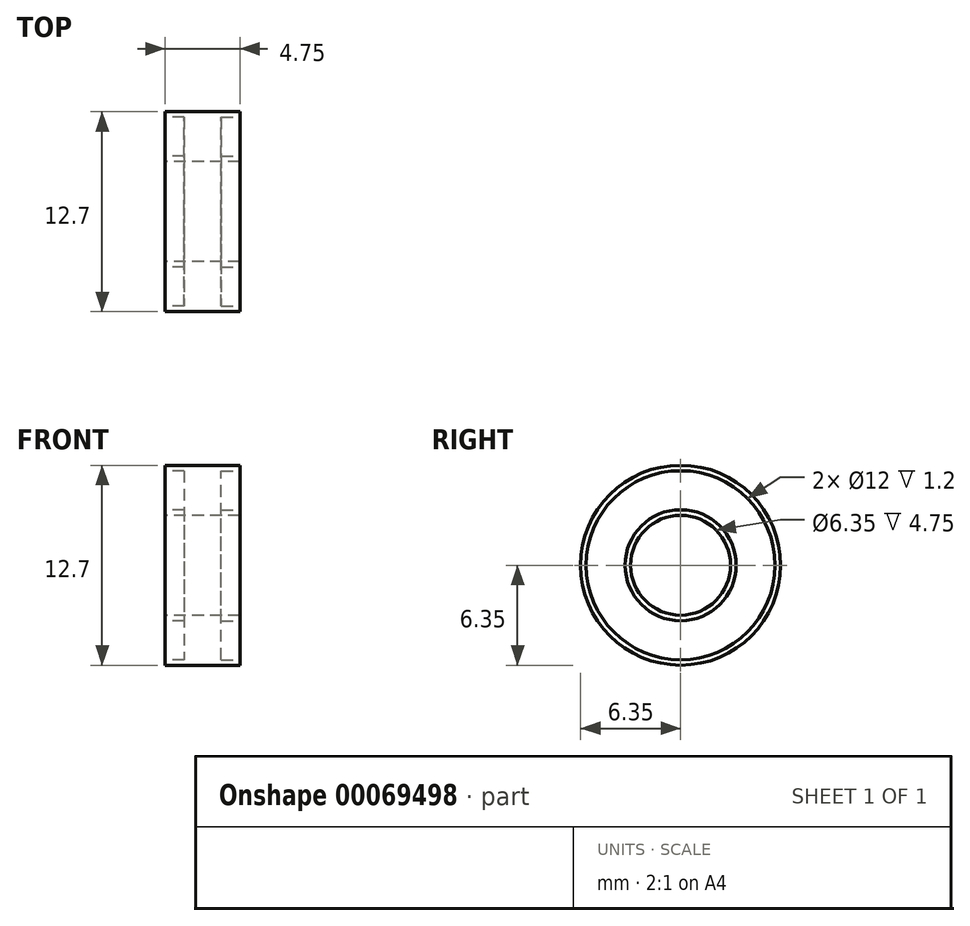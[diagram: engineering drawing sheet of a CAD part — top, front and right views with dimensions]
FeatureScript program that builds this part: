
annotation { "Feature Type Name" : "Feature", "Feature Type Description" : "" }
export const myFeature = defineFeature(function(context is Context, id is Id, definition is map)
    precondition{}
    {
        {
            var Q0;
            Q0=qCreatedBy(makeId("Right.planeOp"),FACE);
            var sketch = newSketch(context, id + "F0", { "sketchPlane" : qUnion([Q0])});
            skCircle(sketch, "E0", {"center": v(0, 0) * mm, "radius": 3.17 * mm});
            skCircle(sketch, "E1", {"center": v(0, 0) * mm, "radius": 6.35 * mm});
            skSolve(sketch);
        }
        {
            var Q0;
            Q0=makeQuery(id+"F0.imprint","IMPRINT",FACE,{"disambiguationData":[TD([[makeQuery(id+"F0.imprint","IMPRINT",EDGE,{"derivedFrom":sQuery(id+"F0.wireOp",EDGE,"E0")}),-1.0]])]});
            extrude(context, id + "F1", {"entities" : qUnion([Q0]), "depth" : 4.75 * mm});
        }
        {
            var Q0;
            Q0=makeQuery(id+"F1.opExtrude","CAP_FACE",FACE,{"disambiguationData":[OSD([sQuery(id+"F0.wireOp",EDGE,"E0"),sQuery(id+"F0.wireOp",EDGE,"E1")])],"isStart":false});
            var sketch = newSketch(context, id + "F2", { "sketchPlane" : qUnion([Q0])});
            skCircle(sketch, "E2", {"center": v(0, 0) * mm, "radius": 3.52 * mm});
            skCircle(sketch, "E3", {"center": v(0, 0) * mm, "radius": 6 * mm});
            skSolve(sketch);
        }
        {
            var Q0;
            Q0=makeQuery(id+"F2.imprint","IMPRINT",FACE,{"disambiguationData":[TD([[makeQuery(id+"F2.imprint","IMPRINT",EDGE,{"derivedFrom":sQuery(id+"F2.wireOp",EDGE,"E2")}),-1.0]])]});
            extrude(context, id + "F3", {"entities" : qUnion([Q0]), "operationType" : NewBodyOperationType.REMOVE, "oppositeDirection" : true, "depth" : 1.2 * mm});
        }
        {
            var Q0;
            Q0=makeQuery(id+"F1.opExtrude","CAP_FACE",FACE,{"disambiguationData":[OSD([sQuery(id+"F0.wireOp",EDGE,"E0"),sQuery(id+"F0.wireOp",EDGE,"E1")])],"isStart":true});
            var sketch = newSketch(context, id + "F4", { "sketchPlane" : qUnion([Q0])});
            skCircle(sketch, "E4", {"center": v(0, 0) * mm, "radius": 3.52 * mm});
            skCircle(sketch, "E5", {"center": v(0, 0) * mm, "radius": 6 * mm});
            skSolve(sketch);
        }
        {
            var Q0;
            Q0=qSketchRegion(id+"F4",true);
            extrude(context, id + "F5", {"entities" : qUnion([Q0]), "operationType" : NewBodyOperationType.REMOVE, "oppositeDirection" : true, "depth" : 1.2 * mm});
        }
    });
